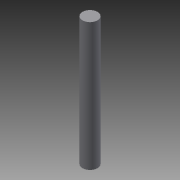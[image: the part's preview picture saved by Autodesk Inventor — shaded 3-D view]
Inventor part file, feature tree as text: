
AUTODESK INVENTOR PART (.ipt)
format: ipt  version: 2015 (Build 190159000, 159)  size: 63,488 bytes
history: native  units: in
note: dims shown in document units (in); Inventor stores cm internally (conversion verified against a paired STEP export)
features: extrude x1, sketch x1
ambient origin geometry x8: Origin, YZ Plane, XZ Plane, XY Plane, X Axis, Y Axis, Z Axis, Center Point
bodies: Solid1 (feature_tree)
feature tree (2):
  extrude  "Extrusion1"  Depth=23.622in TaperAngle=0.0deg
  sketch  "Sketch1"  dims[d0=2.7559in d1=23.622in d2=0.0in]
